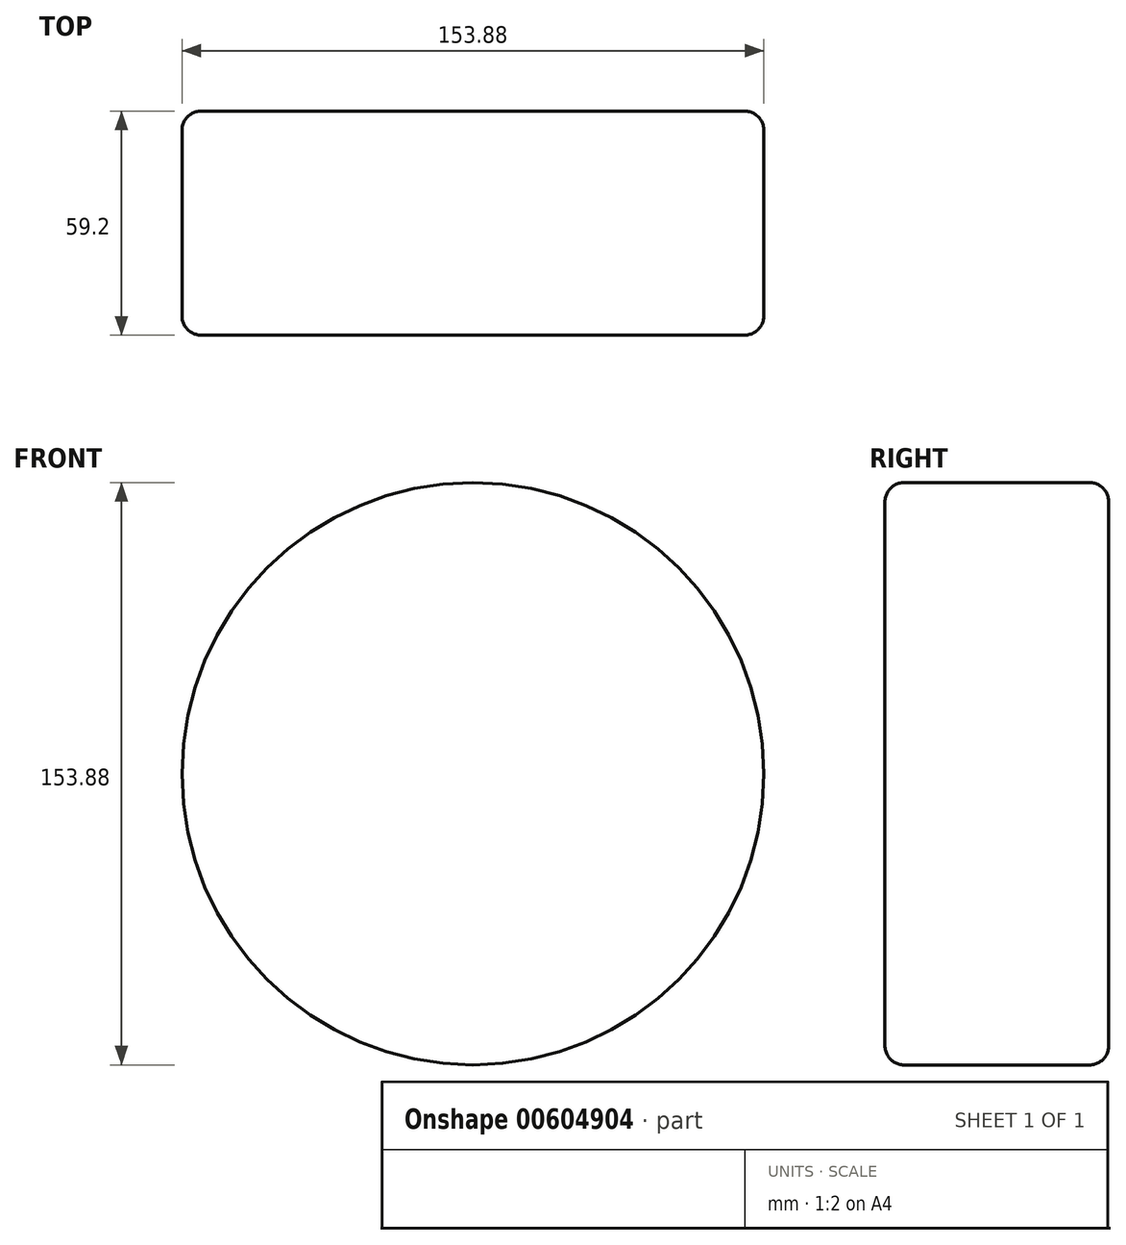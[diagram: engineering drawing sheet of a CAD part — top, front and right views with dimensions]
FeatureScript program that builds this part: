
annotation { "Feature Type Name" : "Feature", "Feature Type Description" : "" }
export const myFeature = defineFeature(function(context is Context, id is Id, definition is map)
    precondition{}
    {
        {
            var Q0;
            Q0=qCreatedBy(makeId("Front.planeOp"),FACE);
            var sketch = newSketch(context, id + "F0", { "sketchPlane" : qUnion([Q0])});
            skCircle(sketch, "E0", {"center": v(0, 0) * mm, "radius": 76.94 * mm});
            skSolve(sketch);
        }
        {
            var Q0;
            Q0=makeQuery(id+"F0.imprint","IMPRINT",FACE,{"disambiguationData":[TD([[makeQuery(id+"F0.imprint","IMPRINT",EDGE,{"derivedFrom":sQuery(id+"F0.wireOp",EDGE,"E0")}),1.0]])]});
            var Q1;
            Q1=makeQuery(id+"F0.imprint","IMPRINT",FACE,{"disambiguationData":[TD([[makeQuery(id+"F0.imprint","IMPRINT",EDGE,{"derivedFrom":sQuery(id+"F0.wireOp",EDGE,"E0")}),1.0]])]});
            extrude(context, id + "F1", {"entities" : qUnion([Q0, Q1]), "depth" : 59.2 * mm, "offsetDistance" : 25.4 * mm});
        }
        {
            var Q0;
            Q0=makeQuery(id+"F1.opExtrude","SWEPT_FACE",FACE,{"disambiguationData":[OSD([sQuery(id+"F0.wireOp",EDGE,"E0")])]});
            fillet(context, id + "F2", {"entities" : qUnion([Q0]), "radius" : 5.08 * mm, "tangentPropagation" : true, "allowEdgeOverflow" : false});
        }
    });
